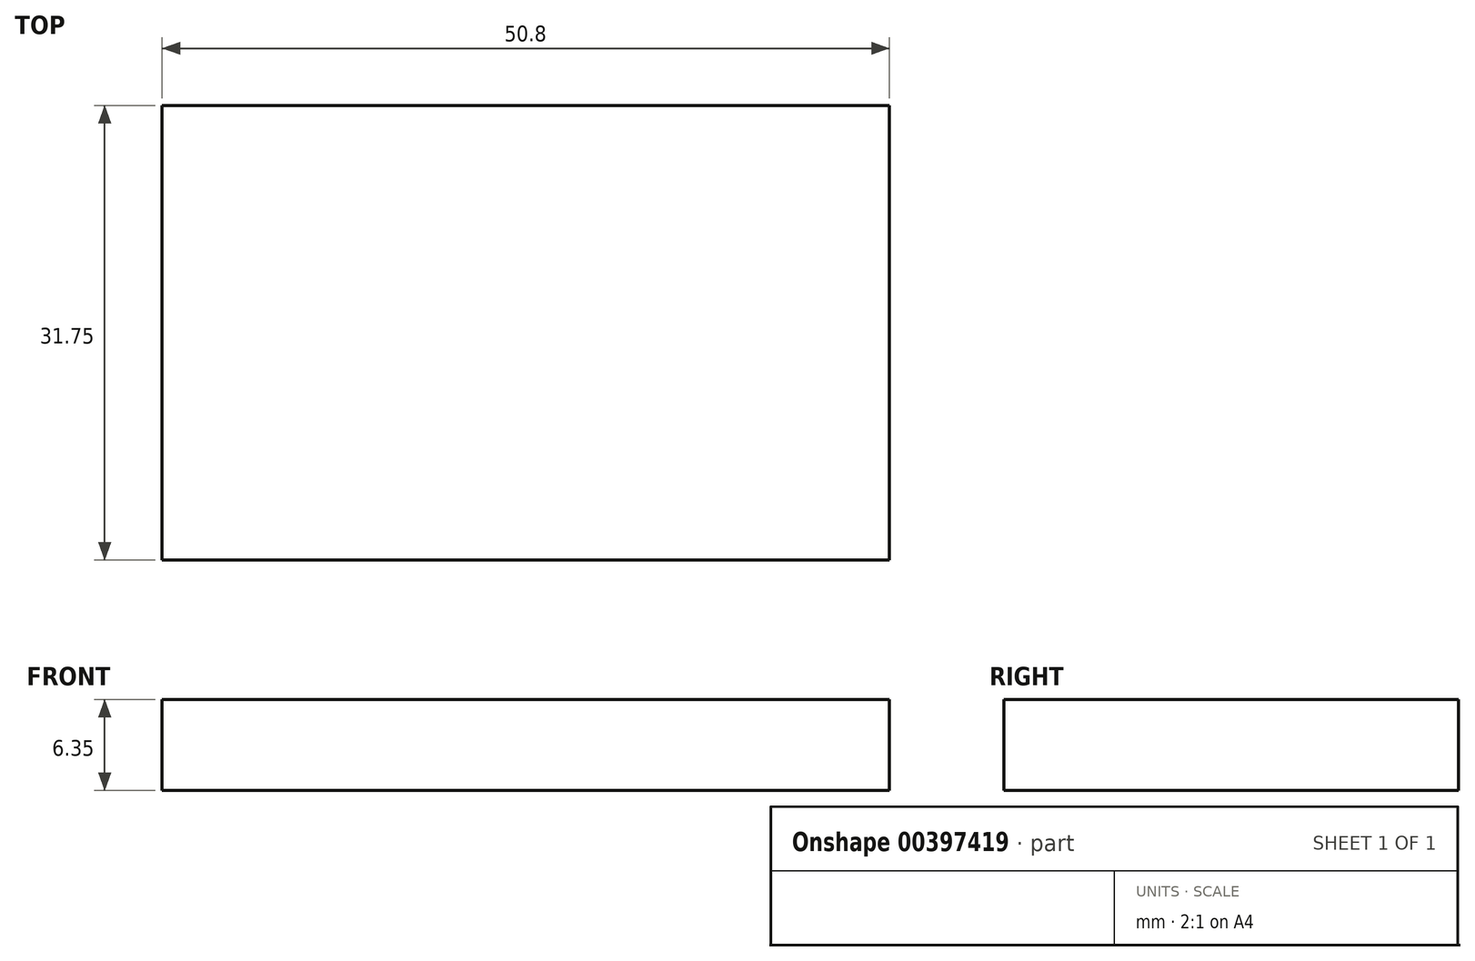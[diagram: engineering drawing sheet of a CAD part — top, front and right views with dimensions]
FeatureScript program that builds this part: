
annotation { "Feature Type Name" : "Feature", "Feature Type Description" : "" }
export const myFeature = defineFeature(function(context is Context, id is Id, definition is map)
    precondition{}
    {
        {
            var Q0;
            Q0=qCreatedBy(makeId("Top.planeOp"),FACE);
            var sketch = newSketch(context, id + "F0", { "sketchPlane" : qUnion([Q0])});
            skLineSegment(sketch, "E0.bottom", {"start": v(0, 31.75) * mm, "end": v(50.8, 31.75) * mm});
            skLineSegment(sketch, "E0.top", {"start": v(0, 0) * mm, "end": v(50.8, 0) * mm});
            skLineSegment(sketch, "E0.left", {"start": v(0, 31.75) * mm, "end": v(0, 0) * mm});
            skLineSegment(sketch, "E0.right", {"start": v(50.8, 31.75) * mm, "end": v(50.8, 0) * mm});
            skSolve(sketch);
        }
        {
            var Q0;
            Q0 = qSketchRegion(id + "F0", true);
            extrude(context, id + "F1", {"entities" : qUnion([Q0]), "depth" : 6.35 * mm});
        }
    });
